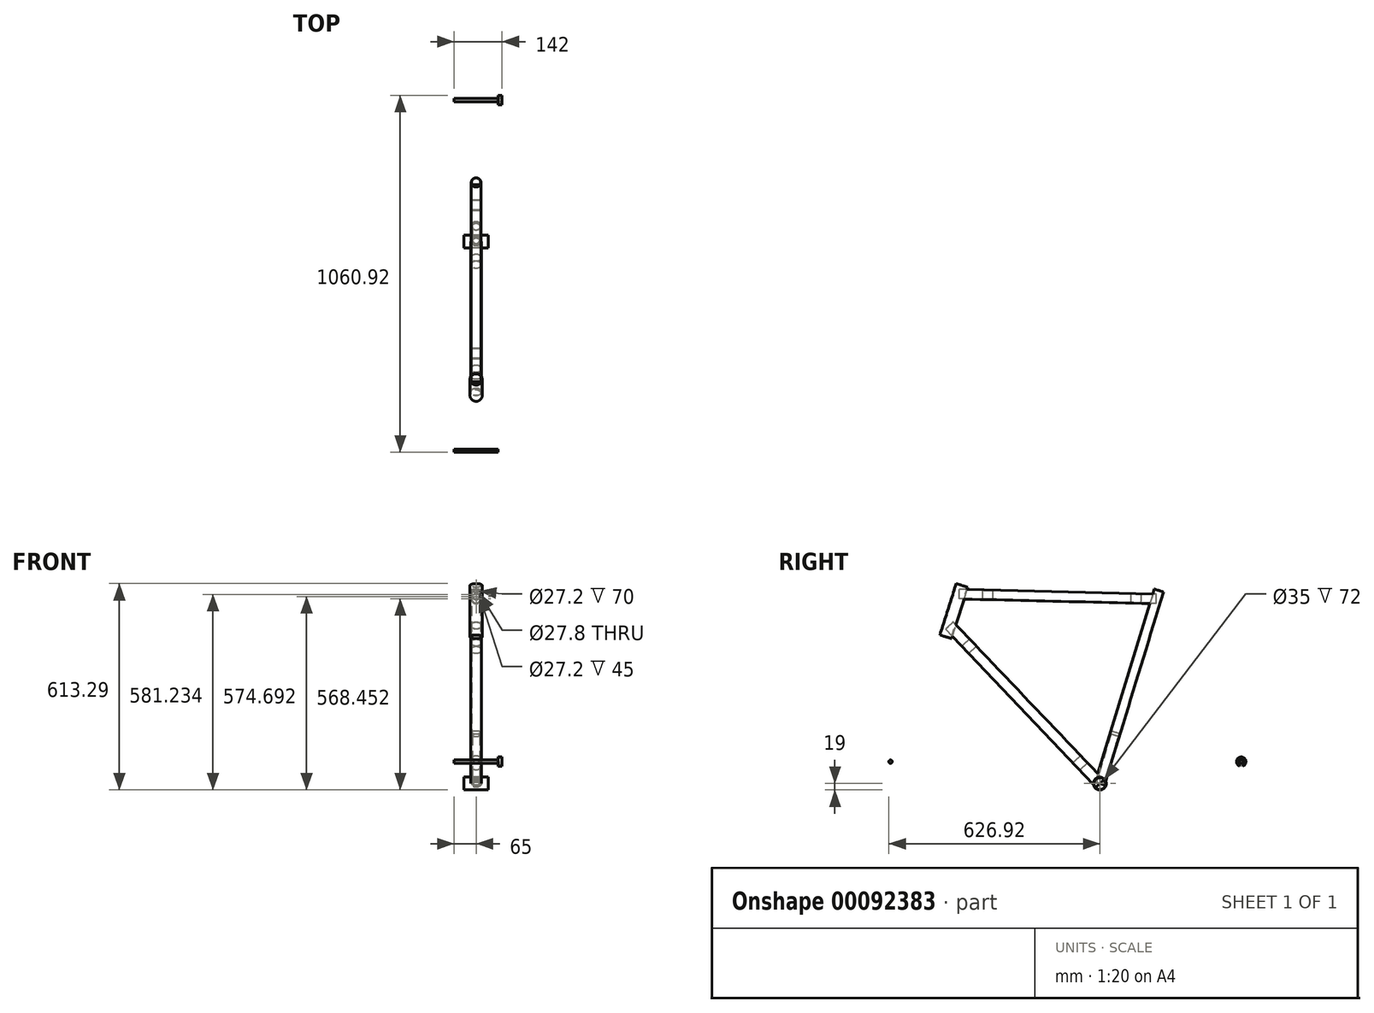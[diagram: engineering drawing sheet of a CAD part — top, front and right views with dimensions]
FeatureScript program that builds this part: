
annotation { "Feature Type Name" : "Feature", "Feature Type Description" : "" }
export const myFeature = defineFeature(function(context is Context, id is Id, definition is map)
    precondition{}
    {
        {
            var Q0;
            Q0=qCreatedBy(makeId("Right.planeOp"),FACE);
            var sketch = newSketch(context, id + "F0", { "sketchPlane" : qUnion([Q0])});
            skLineSegment(sketch, "E0", {"start": v(175.42, 508.78) * mm, "end": v(-409.58, 523.82) * mm});
            skLineSegment(sketch, "E1", {"start": v(-409.58, 523.82) * mm, "end": v(-457.69, 371.22) * mm});
            skLineSegment(sketch, "E2", {"start": v(175.42, 508.78) * mm, "end": v(0, -65) * mm});
            skLineSegment(sketch, "E3", {"start": v(0, -65) * mm, "end": v(420, 0) * mm});
            skLineSegment(sketch, "E4", {"start": v(175.42, 508.78) * mm, "end": v(420, 0) * mm});
            skLineSegment(sketch, "E5", {"start": v(-457.69, 371.22) * mm, "end": v(0, -65) * mm});
            skLineSegment(sketch, "E6", {"start": v(-409.58, 523.82) * mm, "end": v(-574.74, 0) * mm, "construction": true});
            skLineSegment(sketch, "E7", {"start": v(-456.76, 523.82) * mm, "end": v(-621.92, 0) * mm, "construction": true});
            skLineSegment(sketch, "E8", {"start": v(-621.92, 0) * mm, "end": v(420, 0) * mm, "construction": true});
            skLineSegment(sketch, "E9", {"start": v(-457.69, 371.22) * mm, "end": v(-461, 360.73) * mm});
            skLineSegment(sketch, "E10", {"start": v(-461, 360.73) * mm, "end": v(-621.92, 0) * mm});
            skLineSegment(sketch, "E11", {"start": v(-409.58, 523.82) * mm, "end": v(-391.53, 581.04) * mm});
            skLineSegment(sketch, "E12", {"start": v(-391.53, 581.04) * mm, "end": v(-654.6, 663.98) * mm, "construction": true});
            skLineSegment(sketch, "E13", {"start": v(-391.53, 581.04) * mm, "end": v(-514.03, 605.96) * mm});
            skCircle(sketch, "E14", {"center": v(-621.92, 0) * mm, "radius": 344 * mm});
            skCircle(sketch, "E15", {"center": v(420, 0) * mm, "radius": 344 * mm});
            skSolve(sketch);
        }
        {
            var Q0;
            Q0=qCreatedBy(makeId("Right.planeOp"),FACE);
            var sketch = newSketch(context, id + "F1", { "sketchPlane" : qUnion([Q0])});
            skLineSegment(sketch, "E16", {"start": v(-426.93, 529.3) * mm, "end": v(-475.05, 376.7) * mm});
            skLineSegment(sketch, "E17", {"start": v(-387.73, 593.1) * mm, "end": v(-482.6, 292.23) * mm, "construction": true});
            skLineSegment(sketch, "E18", {"start": v(-434.15, 628.31) * mm, "end": v(-424.68, 628.31) * mm});
            skLineSegment(sketch, "E19", {"start": v(-409.58, 523.82) * mm, "end": v(-426.93, 529.3) * mm, "construction": true});
            skLineSegment(sketch, "E20", {"start": v(-457.69, 371.22) * mm, "end": v(-475.05, 376.7) * mm, "construction": true});
            skLineSegment(sketch, "E21", {"start": v(-426.93, 529.3) * mm, "end": v(-425.8, 528.93) * mm});
            skLineSegment(sketch, "E22", {"start": v(-425.8, 528.93) * mm, "end": v(-473.9, 376.34) * mm});
            skLineSegment(sketch, "E23", {"start": v(-473.9, 376.34) * mm, "end": v(-475.05, 376.7) * mm});
            skSolve(sketch);
        }
        {
            var Q0;
            Q0=makeQuery(id+"F1.imprint","IMPRINT",FACE,{"disambiguationData":[TD([[makeQuery(id+"F1.imprint","IMPRINT",EDGE,{"derivedFrom":sQuery(id+"F1.wireOp",EDGE,"E16")}),1.0]])]});
            var Q1;
            Q1=sQuery(id+"F1.wireOp",EDGE,"E17");
            revolve(context, id + "F2", {"entities" : qUnion([Q0]), "axis" : qUnion([Q1]), "revolveType" : RevolveType.FULL});
        }
        {
            var Q0;
            Q0=qCreatedBy(makeId("Right.planeOp"),FACE);
            var sketch = newSketch(context, id + "F3", { "sketchPlane" : qUnion([Q0])});
            skCircle(sketch, "E24", {"center": v(0, -65) * mm, "radius": 17.5 * mm});
            skSolve(sketch);
        }
        {
            var Q0;
            Q0=makeQuery(id+"F3.imprint","IMPRINT",FACE,{"disambiguationData":[TD([[makeQuery(id+"F3.imprint","IMPRINT",EDGE,{"derivedFrom":sQuery(id+"F3.wireOp",EDGE,"E24")}),1.0]])]});
            var Q1;
            Q1=sQuery(id+"F3.wireOp",EDGE,"E24");
            extrude(context, id + "F4", {"entities" : qUnion([Q0]), "surfaceEntities" : qUnion([Q1]), "depth" : 72 * mm, "symmetric" : true});
        }
        {
            var Q0;
            Q0=makeQuery(id+"F4.opExtrude","CAP_FACE",FACE,{"disambiguationData":[OSD([sQuery(id+"F3.wireOp",EDGE,"E24")])],"isStart":false});
            var Q1;
            Q1=makeQuery(id+"F4.opExtrude","CAP_FACE",FACE,{"disambiguationData":[OSD([sQuery(id+"F3.wireOp",EDGE,"E24")])],"isStart":true});
            shell(context, id + "F5", {"entities" : qUnion([Q0, Q1]), "thickness" : 1.5 * mm, "oppositeDirection" : true});
        }
        {
            var Q0;
            Q0=qCreatedBy(makeId("Right.planeOp"),FACE);
            var sketch = newSketch(context, id + "F6", { "sketchPlane" : qUnion([Q0])});
            skLineSegment(sketch, "E25", {"start": v(-27.84, -156.08) * mm, "end": v(195.05, 572.96) * mm, "construction": true});
            skLineSegment(sketch, "E26", {"start": v(175.42, 508.78) * mm, "end": v(161.75, 512.96) * mm, "construction": true});
            skLineSegment(sketch, "E27", {"start": v(0, -65) * mm, "end": v(-47.6, -50.45) * mm, "construction": true});
            skLineSegment(sketch, "E28", {"start": v(161.75, 512.96) * mm, "end": v(-13.68, -60.82) * mm});
            skPoint(sketch, "E28.endSnap0", {"position": v(-13.68, -60.82) * mm});
            skLineSegment(sketch, "E29", {"start": v(161.75, 512.96) * mm, "end": v(162.32, 512.79) * mm});
            skLineSegment(sketch, "E30", {"start": v(162.32, 512.79) * mm, "end": v(115.54, 359.78) * mm});
            skLineSegment(sketch, "E31", {"start": v(115.54, 359.78) * mm, "end": v(106.58, 331.15) * mm});
            skLineSegment(sketch, "E32", {"start": v(106.58, 331.15) * mm, "end": v(33.18, 91.08) * mm});
            skLineSegment(sketch, "E33", {"start": v(33.18, 91.08) * mm, "end": v(33.18, 81.7) * mm});
            skLineSegment(sketch, "E34", {"start": v(33.18, 81.7) * mm, "end": v(-10.67, -61.74) * mm});
            skLineSegment(sketch, "E35", {"start": v(-10.67, -61.74) * mm, "end": v(-13.68, -60.82) * mm});
            skSolve(sketch);
        }
        {
            var Q0;
            Q0 = qSketchRegion(id + "F6", true);
            var Q1;
            Q1=sQuery(id+"F6.wireOp",EDGE,"E25");
            revolve(context, id + "F7", {"operationType" : NewBodyOperationType.ADD, "entities" : qUnion([Q0]), "axis" : qUnion([Q1]), "revolveType" : RevolveType.FULL});
        }
        {
            var Q0;
            Q0=qCreatedBy(makeId("Right.planeOp"),FACE);
            var sketch = newSketch(context, id + "F8", { "sketchPlane" : qUnion([Q0])});
            skLineSegment(sketch, "E36", {"start": v(0, -65) * mm, "end": v(-447.17, 404.6) * mm, "construction": true});
            skLineSegment(sketch, "E37", {"start": v(-447.17, 404.6) * mm, "end": v(-435.69, 415.53) * mm, "construction": true});
            skLineSegment(sketch, "E38", {"start": v(-435.69, 415.53) * mm, "end": v(11.48, -54.07) * mm});
            skLineSegment(sketch, "E39", {"start": v(0, -65) * mm, "end": v(11.48, -54.07) * mm});
            skLineSegment(sketch, "E40", {"start": v(-435.69, 415.53) * mm, "end": v(-436.2, 415.05) * mm});
            skLineSegment(sketch, "E41", {"start": v(-436.2, 415.05) * mm, "end": v(-387.92, 364.36) * mm});
            skLineSegment(sketch, "E42", {"start": v(-387.92, 364.36) * mm, "end": v(-367.02, 342.84) * mm});
            skLineSegment(sketch, "E43", {"start": v(-367.02, 342.84) * mm, "end": v(-57.77, 18.07) * mm});
            skLineSegment(sketch, "E44", {"start": v(-57.77, 18.07) * mm, "end": v(-37.3, -3.86) * mm});
            skLineSegment(sketch, "E45", {"start": v(-37.3, -3.86) * mm, "end": v(10.97, -54.55) * mm});
            skSolve(sketch);
        }
        {
            var Q0;
            Q0 = qSketchRegion(id + "F8", true);
            var Q1;
            Q1=sQuery(id+"F8.wireOp",EDGE,"E36");
            revolve(context, id + "F9", {"entities" : qUnion([Q0]), "axis" : qUnion([Q1]), "revolveType" : RevolveType.FULL});
        }
        {
            var Q0;
            Q0=qCreatedBy(makeId("Right.planeOp"),FACE);
            var sketch = newSketch(context, id + "F10", { "sketchPlane" : qUnion([Q0])});
            skLineSegment(sketch, "E46", {"start": v(-417.7, 498.07) * mm, "end": v(167.82, 483.92) * mm, "construction": true});
            skLineSegment(sketch, "E47", {"start": v(-417.7, 498.07) * mm, "end": v(-417.35, 512.36) * mm});
            skLineSegment(sketch, "E48", {"start": v(-417.35, 512.36) * mm, "end": v(168.17, 498.21) * mm});
            skLineSegment(sketch, "E49", {"start": v(167.82, 483.92) * mm, "end": v(168.17, 498.21) * mm});
            skLineSegment(sketch, "E50", {"start": v(-417.37, 511.67) * mm, "end": v(-347.39, 509.97) * mm});
            skLineSegment(sketch, "E51", {"start": v(-347.39, 509.97) * mm, "end": v(-317.4, 509.55) * mm});
            skLineSegment(sketch, "E52", {"start": v(-317.4, 509.55) * mm, "end": v(93.18, 499.63) * mm});
            skLineSegment(sketch, "E53", {"start": v(93.18, 499.63) * mm, "end": v(123.16, 498.6) * mm});
            skLineSegment(sketch, "E54", {"start": v(123.16, 498.6) * mm, "end": v(168.15, 497.51) * mm});
            skPoint(sketch, "E54.endSnap0", {"position": v(168, 491.07) * mm});
            skSolve(sketch);
        }
        {
            var Q0;
            Q0 = qSketchRegion(id + "F10", true);
            var Q1;
            Q1=sQuery(id+"F10.wireOp",EDGE,"E46");
            revolve(context, id + "F11", {"entities" : qUnion([Q0]), "axis" : qUnion([Q1]), "revolveType" : RevolveType.FULL});
        }
        {
            var Q0;
            Q0=sQuery(id+"F0.wireOp",EDGE,"E3");
            cPlane(context, id + "F12", {"entities" : qUnion([Q0]), "cplaneType" : CPlaneType.LINE_ANGLE, "offset" : 150 * mm, "angle" : 0 * degree, "width" : 150 * mm, "height" : 150 * mm});
        }
        {
            var Q0;
            Q0=qCreatedBy(makeId("Right.planeOp"),FACE);
            cPlane(context, id + "F13", {"entities" : qUnion([Q0]), "cplaneType" : CPlaneType.OFFSET, "offset" : 65 * mm, "width" : 150 * mm, "height" : 150 * mm});
        }
        {
            var Q0;
            Q0=qCreatedBy(id+"F13.planeOp",FACE);
            var sketch = newSketch(context, id + "F14", { "sketchPlane" : qUnion([Q0])});
            skArc(sketch, "E55", {"start": v(425, -13.08) * mm, "mid": v(420, 14) * mm, "end": v(415, -13.08) * mm});
            skArc(sketch, "E56", {"start": v(425, 0) * mm, "mid": v(420, 5) * mm, "end": v(415, 0) * mm});
            skLineSegment(sketch, "E57", {"start": v(415, 0) * mm, "end": v(415, -13.08) * mm});
            skLineSegment(sketch, "E58", {"start": v(425, 0) * mm, "end": v(425, -13.08) * mm});
            skSolve(sketch);
        }
        {
            var Q0;
            Q0 = qSketchRegion(id + "F14", true);
            extrude(context, id + "F15", {"entities" : qUnion([Q0]), "depth" : 12 * mm});
        }
        {
            var Q0;
            Q0=makeQuery(id+"F15.opExtrude","CAP_FACE",FACE,{"disambiguationData":[OSD([sQuery(id+"F14.wireOp",EDGE,"E55"),sQuery(id+"F14.wireOp",EDGE,"E56"),sQuery(id+"F14.wireOp",EDGE,"E57"),sQuery(id+"F14.wireOp",EDGE,"E58")])],"isStart":false});
            var Q1;
            Q1=makeQuery(id+"F15.opExtrude","SWEPT_FACE",FACE,{"disambiguationData":[OSD([sQuery(id+"F14.wireOp",EDGE,"E57")])]});
            var Q2;
            Q2=makeQuery(id+"F15.opExtrude","SWEPT_FACE",FACE,{"disambiguationData":[OSD([sQuery(id+"F14.wireOp",EDGE,"E56")])]});
            var Q3;
            Q3=makeQuery(id+"F15.opExtrude","SWEPT_FACE",FACE,{"disambiguationData":[OSD([sQuery(id+"F14.wireOp",EDGE,"E58")])]});
            shell(context, id + "F16", {"entities" : qUnion([Q0, Q1, Q2, Q3]), "thickness" : 3 * mm});
        }
        {
            var Q0;
            Q0=qCreatedBy(makeId("Right.planeOp"),FACE);
            var sketch = newSketch(context, id + "F17", { "sketchPlane" : qUnion([Q0])});
            skCircle(sketch, "E59", {"center": v(-621.92, 0) * mm, "radius": 5 * mm});
            skCircle(sketch, "E60", {"center": v(420, 0) * mm, "radius": 5 * mm});
            skSolve(sketch);
        }
        {
            var Q0;
            Q0 = qSketchRegion(id + "F17", true);
            extrude(context, id + "F18", {"entities" : qUnion([Q0]), "depth" : 130 * mm, "symmetric" : true});
        }
    });
